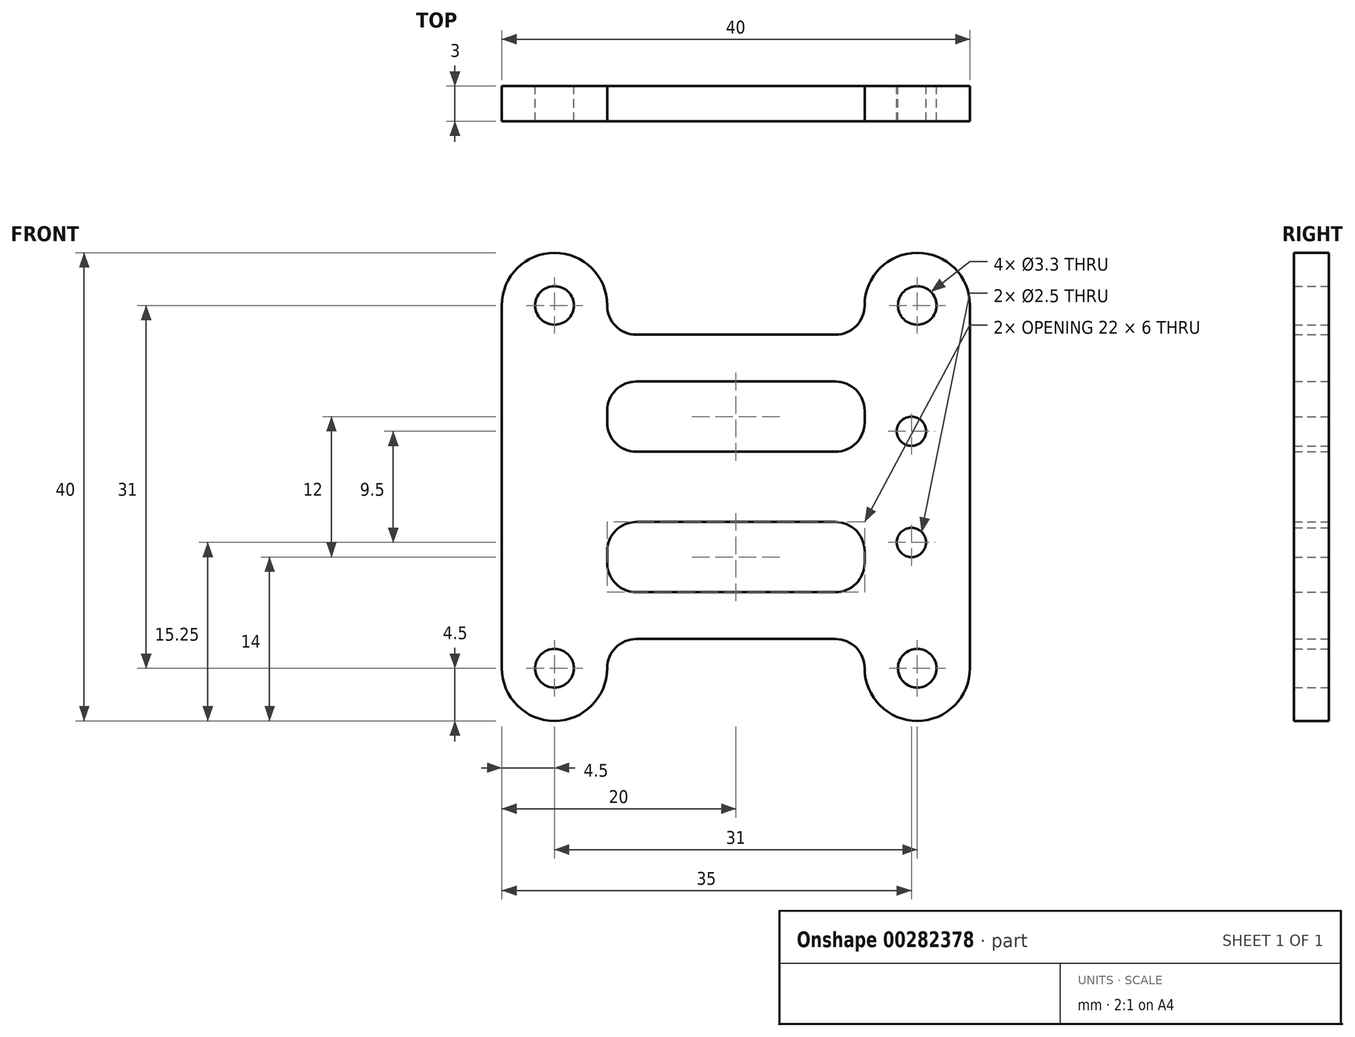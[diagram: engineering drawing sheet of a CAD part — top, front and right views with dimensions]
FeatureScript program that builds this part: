
annotation { "Feature Type Name" : "Feature", "Feature Type Description" : "" }
export const myFeature = defineFeature(function(context is Context, id is Id, definition is map)
    precondition{}
    {
        {
            var Q0;
            Q0=qCreatedBy(makeId("Front.planeOp"),FACE);
            var sketch = newSketch(context, id + "F0", { "sketchPlane" : qUnion([Q0])});
            skLineSegment(sketch, "E0.bottom", {"start": v(11, -15.5) * mm, "end": v(-11, -15.5) * mm, "construction": true});
            skLineSegment(sketch, "E0.top", {"start": v(11, 15.5) * mm, "end": v(-11, 15.5) * mm, "construction": true});
            skPoint(sketch, "E0.middle", {"position": v(0, 0) * mm});
            skCircle(sketch, "E1", {"center": v(-15.5, 15.5) * mm, "radius": 1.65 * mm});
            skArc(sketch, "E2", {"start": v(-11, 15.5) * mm, "mid": v(-15.5, 20) * mm, "end": v(-20, 15.5) * mm});
            skCircle(sketch, "E3", {"center": v(15.5, 15.5) * mm, "radius": 1.65 * mm});
            skArc(sketch, "E4", {"start": v(20, 15.5) * mm, "mid": v(15.5, 20) * mm, "end": v(11, 15.5) * mm});
            skArc(sketch, "E5", {"start": v(11, -15.5) * mm, "mid": v(15.5, -20) * mm, "end": v(20, -15.5) * mm});
            skCircle(sketch, "E6", {"center": v(15.5, -15.5) * mm, "radius": 1.65 * mm});
            skCircle(sketch, "E7", {"center": v(-15.5, -15.5) * mm, "radius": 1.65 * mm});
            skArc(sketch, "E8", {"start": v(-20, -15.5) * mm, "mid": v(-15.5, -20) * mm, "end": v(-11, -15.5) * mm});
            skLineSegment(sketch, "E9", {"start": v(8.5, -3) * mm, "end": v(-8.5, -3) * mm});
            skLineSegment(sketch, "E10", {"start": v(-11, -5.5) * mm, "end": v(-11, -6.5) * mm});
            skLineSegment(sketch, "E11", {"start": v(-8.5, -9) * mm, "end": v(8.5, -9) * mm});
            skLineSegment(sketch, "E12", {"start": v(11, -6.5) * mm, "end": v(11, -5.5) * mm});
            skPoint(sketch, "E13.visualSharp", {"position": v(-11, -3) * mm});
            skArc(sketch, "E13.filletArc", {"start": v(-8.5, -3) * mm, "mid": v(-10.27, -3.73) * mm, "end": v(-11, -5.5) * mm});
            skPoint(sketch, "E14.visualSharp", {"position": v(11, -3) * mm});
            skArc(sketch, "E14.filletArc", {"start": v(11, -5.5) * mm, "mid": v(10.27, -3.73) * mm, "end": v(8.5, -3) * mm});
            skPoint(sketch, "E15.visualSharp", {"position": v(11, -9) * mm});
            skArc(sketch, "E15.filletArc", {"start": v(8.5, -9) * mm, "mid": v(10.27, -8.27) * mm, "end": v(11, -6.5) * mm});
            skPoint(sketch, "E16.visualSharp", {"position": v(-11, -9) * mm});
            skArc(sketch, "E16.filletArc", {"start": v(-11, -6.5) * mm, "mid": v(-10.27, -8.27) * mm, "end": v(-8.5, -9) * mm});
            skLineSegment(sketch, "E17", {"start": v(15.5, 15.5) * mm, "end": v(20, 15.5) * mm, "construction": true});
            skLineSegment(sketch, "E18", {"start": v(20, 15.5) * mm, "end": v(20, -15.5) * mm});
            skLineSegment(sketch, "E19", {"start": v(-11, 15.5) * mm, "end": v(-11, 15.5) * mm});
            skLineSegment(sketch, "E20", {"start": v(-8.5, 13) * mm, "end": v(8.5, 13) * mm});
            skLineSegment(sketch, "E21", {"start": v(11, 15.5) * mm, "end": v(11, 15.5) * mm});
            skLineSegment(sketch, "E22", {"start": v(-11, -15.5) * mm, "end": v(-11, -15.5) * mm});
            skLineSegment(sketch, "E23", {"start": v(-8.5, -13) * mm, "end": v(8.5, -13) * mm});
            skLineSegment(sketch, "E24", {"start": v(11, -15.5) * mm, "end": v(11, -15.5) * mm});
            skPoint(sketch, "E25.visualSharp", {"position": v(-11, 13) * mm});
            skArc(sketch, "E25.filletArc", {"start": v(-11, 15.5) * mm, "mid": v(-10.27, 13.73) * mm, "end": v(-8.5, 13) * mm});
            skPoint(sketch, "E26.visualSharp", {"position": v(11, 13) * mm});
            skArc(sketch, "E26.filletArc", {"start": v(8.5, 13) * mm, "mid": v(10.27, 13.73) * mm, "end": v(11, 15.5) * mm});
            skPoint(sketch, "E27.visualSharp", {"position": v(-11, -13) * mm});
            skArc(sketch, "E27.filletArc", {"start": v(-8.5, -13) * mm, "mid": v(-10.27, -13.73) * mm, "end": v(-11, -15.5) * mm});
            skPoint(sketch, "E28.visualSharp", {"position": v(11, -13) * mm});
            skArc(sketch, "E28.filletArc", {"start": v(11, -15.5) * mm, "mid": v(10.27, -13.73) * mm, "end": v(8.5, -13) * mm});
            skLineSegment(sketch, "E29", {"start": v(-20, 15.5) * mm, "end": v(-20, -15.5) * mm});
            skLineSegment(sketch, "E30", {"start": v(-20, 0) * mm, "end": v(20, 0) * mm, "construction": true});
            skLineSegment(sketch, "E31", {"start": v(0, 0) * mm, "end": v(0, 13) * mm, "construction": true});
            skLineSegment(sketch, "E32", {"start": v(-8.5, 13) * mm, "end": v(-8.5, -13) * mm, "construction": true});
            skLineSegment(sketch, "E33", {"start": v(8.5, 13) * mm, "end": v(8.5, -13) * mm, "construction": true});
            skLineSegment(sketch, "E34.MirrorCS", {"start": v(8.5, 3) * mm, "end": v(-8.5, 3) * mm});
            skArc(sketch, "E35.MirrorCS", {"start": v(-8.5, 3) * mm, "mid": v(-10.27, 3.73) * mm, "end": v(-11, 5.5) * mm});
            skArc(sketch, "E36.MirrorCS", {"start": v(-11, 6.5) * mm, "mid": v(-10.27, 8.27) * mm, "end": v(-8.5, 9) * mm});
            skLineSegment(sketch, "E37.MirrorCS", {"start": v(-8.5, 9) * mm, "end": v(8.5, 9) * mm});
            skArc(sketch, "E38.MirrorCS", {"start": v(8.5, 9) * mm, "mid": v(10.27, 8.27) * mm, "end": v(11, 6.5) * mm});
            skArc(sketch, "E39.MirrorCS", {"start": v(11, 5.5) * mm, "mid": v(10.27, 3.73) * mm, "end": v(8.5, 3) * mm});
            skLineSegment(sketch, "E40.MirrorCS", {"start": v(11, 6.5) * mm, "end": v(11, 5.5) * mm});
            skLineSegment(sketch, "E41.MirrorCS", {"start": v(-11, 5.5) * mm, "end": v(-11, 6.5) * mm});
            skLineSegment(sketch, "E42", {"start": v(15, 0) * mm, "end": v(15, 4.75) * mm, "construction": true});
            skLineSegment(sketch, "E43", {"start": v(15, 0) * mm, "end": v(15, -4.75) * mm, "construction": true});
            skCircle(sketch, "E44", {"center": v(15, 4.75) * mm, "radius": 1.25 * mm});
            skCircle(sketch, "E45", {"center": v(15, -4.75) * mm, "radius": 1.25 * mm});
            skSolve(sketch);
        }
        {
            var Q0;
            Q0=qSketchRegion(id+"F0",true);
            extrude(context, id + "F1", {"entities" : qUnion([Q0]), "depth" : 3 * mm});
        }
    });
